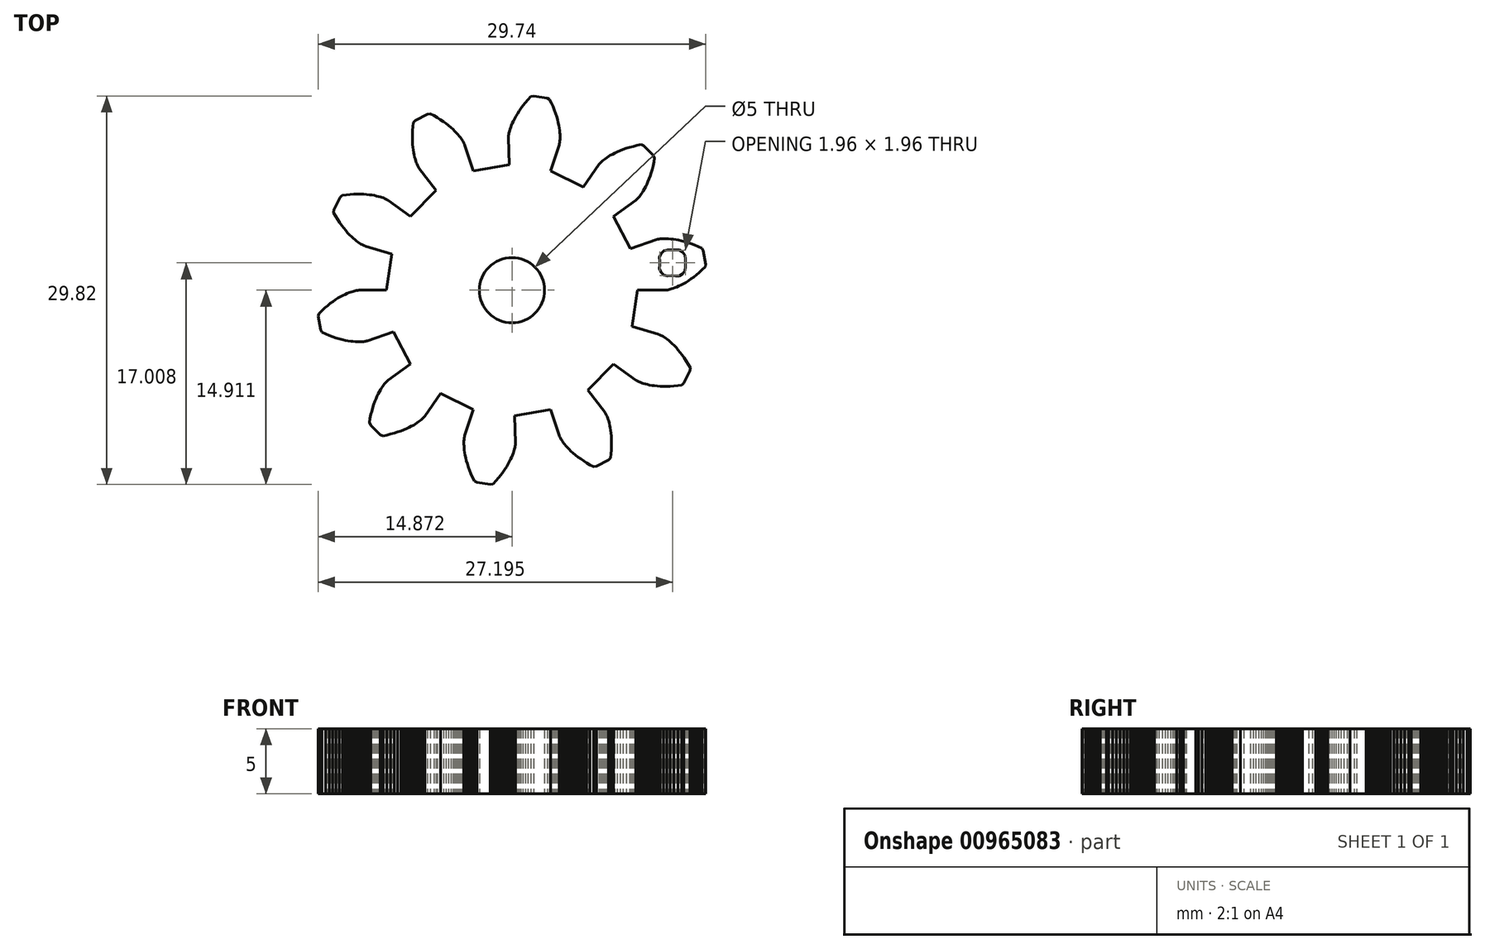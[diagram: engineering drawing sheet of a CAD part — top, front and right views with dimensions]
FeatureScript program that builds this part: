
annotation { "Feature Type Name" : "Feature", "Feature Type Description" : "" }
export const myFeature = defineFeature(function(context is Context, id is Id, definition is map)
    precondition{}
    {
        {
            var Q0;
            Q0=qCreatedBy(makeId("Top.planeOp"),FACE);
            var sketch = newSketch(context, id + "F0", { "sketchPlane" : qUnion([Q0])});
            skLineSegment(sketch, "E0", {"start": v(14.04, 3.47) * mm, "end": v(16.16, 3.47) * mm});
            skLineSegment(sketch, "E1", {"start": v(16.16, 3.47) * mm, "end": v(16.17, 3.47) * mm});
            skLineSegment(sketch, "E2", {"start": v(16.17, 3.47) * mm, "end": v(16.2, 3.47) * mm});
            skLineSegment(sketch, "E3", {"start": v(16.2, 3.47) * mm, "end": v(16.25, 3.48) * mm});
            skLineSegment(sketch, "E4", {"start": v(16.25, 3.48) * mm, "end": v(16.3, 3.49) * mm});
            skLineSegment(sketch, "E5", {"start": v(16.3, 3.49) * mm, "end": v(16.37, 3.5) * mm});
            skLineSegment(sketch, "E6", {"start": v(16.37, 3.5) * mm, "end": v(16.46, 3.52) * mm});
            skLineSegment(sketch, "E7", {"start": v(16.46, 3.52) * mm, "end": v(16.55, 3.54) * mm});
            skLineSegment(sketch, "E8", {"start": v(16.55, 3.54) * mm, "end": v(16.66, 3.57) * mm});
            skLineSegment(sketch, "E9", {"start": v(16.66, 3.57) * mm, "end": v(16.79, 3.61) * mm});
            skLineSegment(sketch, "E10", {"start": v(16.79, 3.61) * mm, "end": v(16.92, 3.66) * mm});
            skLineSegment(sketch, "E11", {"start": v(16.92, 3.66) * mm, "end": v(17.07, 3.72) * mm});
            skLineSegment(sketch, "E12", {"start": v(17.07, 3.72) * mm, "end": v(17.22, 3.8) * mm});
            skLineSegment(sketch, "E13", {"start": v(17.22, 3.8) * mm, "end": v(17.4, 3.87) * mm});
            skLineSegment(sketch, "E14", {"start": v(17.4, 3.87) * mm, "end": v(17.57, 3.97) * mm});
            skLineSegment(sketch, "E15", {"start": v(17.57, 3.97) * mm, "end": v(17.75, 4.07) * mm});
            skLineSegment(sketch, "E16", {"start": v(17.75, 4.07) * mm, "end": v(17.95, 4.2) * mm});
            skLineSegment(sketch, "E17", {"start": v(17.95, 4.2) * mm, "end": v(18.15, 4.33) * mm});
            skLineSegment(sketch, "E18", {"start": v(18.15, 4.33) * mm, "end": v(18.36, 4.48) * mm});
            skLineSegment(sketch, "E19", {"start": v(18.36, 4.48) * mm, "end": v(18.57, 4.65) * mm});
            skLineSegment(sketch, "E20", {"start": v(18.57, 4.65) * mm, "end": v(18.8, 4.83) * mm});
            skLineSegment(sketch, "E21", {"start": v(18.8, 4.83) * mm, "end": v(19.01, 5.04) * mm});
            skLineSegment(sketch, "E22", {"start": v(19.01, 5.04) * mm, "end": v(19.24, 5.25) * mm});
            skLineSegment(sketch, "E23", {"start": v(19.24, 5.25) * mm, "end": v(19.28, 5.47) * mm});
            skLineSegment(sketch, "E24", {"start": v(19.28, 5.47) * mm, "end": v(19.1, 6.5) * mm});
            skLineSegment(sketch, "E25", {"start": v(19.1, 6.5) * mm, "end": v(19, 6.7) * mm});
            skLineSegment(sketch, "E26", {"start": v(19, 6.7) * mm, "end": v(18.71, 6.82) * mm});
            skLineSegment(sketch, "E27", {"start": v(18.71, 6.82) * mm, "end": v(18.43, 6.94) * mm});
            skLineSegment(sketch, "E28", {"start": v(18.43, 6.94) * mm, "end": v(18.17, 7.04) * mm});
            skLineSegment(sketch, "E29", {"start": v(18.17, 7.04) * mm, "end": v(17.9, 7.13) * mm});
            skLineSegment(sketch, "E30", {"start": v(17.9, 7.13) * mm, "end": v(17.66, 7.2) * mm});
            skLineSegment(sketch, "E31", {"start": v(17.66, 7.2) * mm, "end": v(17.43, 7.26) * mm});
            skLineSegment(sketch, "E32", {"start": v(17.43, 7.26) * mm, "end": v(17.2, 7.31) * mm});
            skLineSegment(sketch, "E33", {"start": v(17.2, 7.31) * mm, "end": v(17, 7.35) * mm});
            skLineSegment(sketch, "E34", {"start": v(17, 7.35) * mm, "end": v(16.8, 7.38) * mm});
            skLineSegment(sketch, "E35", {"start": v(16.8, 7.38) * mm, "end": v(16.6, 7.4) * mm});
            skLineSegment(sketch, "E36", {"start": v(16.6, 7.4) * mm, "end": v(16.44, 7.42) * mm});
            skLineSegment(sketch, "E37", {"start": v(16.44, 7.42) * mm, "end": v(16.28, 7.43) * mm});
            skLineSegment(sketch, "E38", {"start": v(16.28, 7.43) * mm, "end": v(16.14, 7.43) * mm});
            skLineSegment(sketch, "E39", {"start": v(16.14, 7.43) * mm, "end": v(16, 7.43) * mm});
            skLineSegment(sketch, "E40", {"start": v(16, 7.43) * mm, "end": v(15.9, 7.42) * mm});
            skLineSegment(sketch, "E41", {"start": v(15.9, 7.42) * mm, "end": v(15.8, 7.41) * mm});
            skLineSegment(sketch, "E42", {"start": v(15.8, 7.41) * mm, "end": v(15.7, 7.4) * mm});
            skLineSegment(sketch, "E43", {"start": v(15.7, 7.4) * mm, "end": v(15.64, 7.39) * mm});
            skLineSegment(sketch, "E44", {"start": v(15.64, 7.39) * mm, "end": v(15.58, 7.38) * mm});
            skLineSegment(sketch, "E45", {"start": v(15.58, 7.38) * mm, "end": v(15.54, 7.37) * mm});
            skLineSegment(sketch, "E46", {"start": v(15.54, 7.37) * mm, "end": v(15.51, 7.36) * mm});
            skLineSegment(sketch, "E47", {"start": v(15.51, 7.36) * mm, "end": v(15.5, 7.36) * mm});
            skLineSegment(sketch, "E48", {"start": v(15.5, 7.36) * mm, "end": v(13.5, 6.65) * mm});
            skLineSegment(sketch, "E49", {"start": v(13.5, 6.65) * mm, "end": v(12.2, 9.13) * mm});
            skLineSegment(sketch, "E50", {"start": v(12.2, 9.13) * mm, "end": v(13.92, 10.38) * mm});
            skLineSegment(sketch, "E51", {"start": v(13.92, 10.38) * mm, "end": v(13.93, 10.39) * mm});
            skLineSegment(sketch, "E52", {"start": v(13.93, 10.39) * mm, "end": v(13.95, 10.4) * mm});
            skLineSegment(sketch, "E53", {"start": v(13.95, 10.4) * mm, "end": v(13.98, 10.43) * mm});
            skLineSegment(sketch, "E54", {"start": v(13.98, 10.43) * mm, "end": v(14.02, 10.47) * mm});
            skLineSegment(sketch, "E55", {"start": v(14.02, 10.47) * mm, "end": v(14.07, 10.52) * mm});
            skLineSegment(sketch, "E56", {"start": v(14.07, 10.52) * mm, "end": v(14.13, 10.59) * mm});
            skLineSegment(sketch, "E57", {"start": v(14.13, 10.59) * mm, "end": v(14.2, 10.66) * mm});
            skLineSegment(sketch, "E58", {"start": v(14.2, 10.66) * mm, "end": v(14.26, 10.75) * mm});
            skLineSegment(sketch, "E59", {"start": v(14.26, 10.75) * mm, "end": v(14.34, 10.86) * mm});
            skLineSegment(sketch, "E60", {"start": v(14.34, 10.86) * mm, "end": v(14.42, 10.98) * mm});
            skLineSegment(sketch, "E61", {"start": v(14.42, 10.98) * mm, "end": v(14.5, 11.11) * mm});
            skLineSegment(sketch, "E62", {"start": v(14.5, 11.11) * mm, "end": v(14.59, 11.26) * mm});
            skLineSegment(sketch, "E63", {"start": v(14.59, 11.26) * mm, "end": v(14.68, 11.42) * mm});
            skLineSegment(sketch, "E64", {"start": v(14.68, 11.42) * mm, "end": v(14.76, 11.6) * mm});
            skLineSegment(sketch, "E65", {"start": v(14.76, 11.6) * mm, "end": v(14.85, 11.8) * mm});
            skLineSegment(sketch, "E66", {"start": v(14.85, 11.8) * mm, "end": v(14.94, 12.01) * mm});
            skLineSegment(sketch, "E67", {"start": v(14.94, 12.01) * mm, "end": v(15.02, 12.24) * mm});
            skLineSegment(sketch, "E68", {"start": v(15.02, 12.24) * mm, "end": v(15.1, 12.49) * mm});
            skLineSegment(sketch, "E69", {"start": v(15.1, 12.49) * mm, "end": v(15.17, 12.75) * mm});
            skLineSegment(sketch, "E70", {"start": v(15.17, 12.75) * mm, "end": v(15.24, 13.03) * mm});
            skLineSegment(sketch, "E71", {"start": v(15.24, 13.03) * mm, "end": v(15.3, 13.32) * mm});
            skLineSegment(sketch, "E72", {"start": v(15.3, 13.32) * mm, "end": v(15.36, 13.63) * mm});
            skLineSegment(sketch, "E73", {"start": v(15.36, 13.63) * mm, "end": v(15.27, 13.82) * mm});
            skLineSegment(sketch, "E74", {"start": v(15.27, 13.82) * mm, "end": v(14.51, 14.56) * mm});
            skLineSegment(sketch, "E75", {"start": v(14.51, 14.56) * mm, "end": v(14.32, 14.65) * mm});
            skLineSegment(sketch, "E76", {"start": v(14.32, 14.65) * mm, "end": v(14, 14.59) * mm});
            skLineSegment(sketch, "E77", {"start": v(14, 14.59) * mm, "end": v(13.72, 14.52) * mm});
            skLineSegment(sketch, "E78", {"start": v(13.72, 14.52) * mm, "end": v(13.44, 14.44) * mm});
            skLineSegment(sketch, "E79", {"start": v(13.44, 14.44) * mm, "end": v(13.18, 14.36) * mm});
            skLineSegment(sketch, "E80", {"start": v(13.18, 14.36) * mm, "end": v(12.94, 14.28) * mm});
            skLineSegment(sketch, "E81", {"start": v(12.94, 14.28) * mm, "end": v(12.71, 14.19) * mm});
            skLineSegment(sketch, "E82", {"start": v(12.71, 14.19) * mm, "end": v(12.5, 14.1) * mm});
            skLineSegment(sketch, "E83", {"start": v(12.5, 14.1) * mm, "end": v(12.3, 14) * mm});
            skLineSegment(sketch, "E84", {"start": v(12.3, 14) * mm, "end": v(12.13, 13.91) * mm});
            skLineSegment(sketch, "E85", {"start": v(12.13, 13.91) * mm, "end": v(11.97, 13.82) * mm});
            skLineSegment(sketch, "E86", {"start": v(11.97, 13.82) * mm, "end": v(11.82, 13.73) * mm});
            skLineSegment(sketch, "E87", {"start": v(11.82, 13.73) * mm, "end": v(11.69, 13.65) * mm});
            skLineSegment(sketch, "E88", {"start": v(11.69, 13.65) * mm, "end": v(11.57, 13.57) * mm});
            skLineSegment(sketch, "E89", {"start": v(11.57, 13.57) * mm, "end": v(11.47, 13.49) * mm});
            skLineSegment(sketch, "E90", {"start": v(11.47, 13.49) * mm, "end": v(11.38, 13.42) * mm});
            skLineSegment(sketch, "E91", {"start": v(11.38, 13.42) * mm, "end": v(11.3, 13.35) * mm});
            skLineSegment(sketch, "E92", {"start": v(11.3, 13.35) * mm, "end": v(11.24, 13.29) * mm});
            skLineSegment(sketch, "E93", {"start": v(11.24, 13.29) * mm, "end": v(11.2, 13.24) * mm});
            skLineSegment(sketch, "E94", {"start": v(11.2, 13.24) * mm, "end": v(11.15, 13.2) * mm});
            skLineSegment(sketch, "E95", {"start": v(11.15, 13.2) * mm, "end": v(11.12, 13.16) * mm});
            skLineSegment(sketch, "E96", {"start": v(11.12, 13.16) * mm, "end": v(11.1, 13.14) * mm});
            skLineSegment(sketch, "E97", {"start": v(11.1, 13.14) * mm, "end": v(11.1, 13.13) * mm});
            skLineSegment(sketch, "E98", {"start": v(11.1, 13.13) * mm, "end": v(9.9, 11.39) * mm});
            skLineSegment(sketch, "E99", {"start": v(9.9, 11.39) * mm, "end": v(7.39, 12.63) * mm});
            skLineSegment(sketch, "E100", {"start": v(7.39, 12.63) * mm, "end": v(8.04, 14.64) * mm});
            skLineSegment(sketch, "E101", {"start": v(8.04, 14.64) * mm, "end": v(8.05, 14.66) * mm});
            skLineSegment(sketch, "E102", {"start": v(8.05, 14.66) * mm, "end": v(8.05, 14.69) * mm});
            skLineSegment(sketch, "E103", {"start": v(8.05, 14.69) * mm, "end": v(8.06, 14.73) * mm});
            skLineSegment(sketch, "E104", {"start": v(8.06, 14.73) * mm, "end": v(8.07, 14.78) * mm});
            skLineSegment(sketch, "E105", {"start": v(8.07, 14.78) * mm, "end": v(8.08, 14.86) * mm});
            skLineSegment(sketch, "E106", {"start": v(8.08, 14.86) * mm, "end": v(8.1, 14.94) * mm});
            skLineSegment(sketch, "E107", {"start": v(8.1, 14.94) * mm, "end": v(8.1, 15.04) * mm});
            skLineSegment(sketch, "E108", {"start": v(8.1, 15.04) * mm, "end": v(8.1, 15.15) * mm});
            skLineSegment(sketch, "E109", {"start": v(8.1, 15.15) * mm, "end": v(8.1, 15.28) * mm});
            skLineSegment(sketch, "E110", {"start": v(8.1, 15.28) * mm, "end": v(8.1, 15.43) * mm});
            skLineSegment(sketch, "E111", {"start": v(8.1, 15.43) * mm, "end": v(8.09, 15.58) * mm});
            skLineSegment(sketch, "E112", {"start": v(8.09, 15.58) * mm, "end": v(8.07, 15.75) * mm});
            skLineSegment(sketch, "E113", {"start": v(8.07, 15.75) * mm, "end": v(8.04, 15.94) * mm});
            skLineSegment(sketch, "E114", {"start": v(8.04, 15.94) * mm, "end": v(8, 16.14) * mm});
            skLineSegment(sketch, "E115", {"start": v(8, 16.14) * mm, "end": v(7.96, 16.35) * mm});
            skLineSegment(sketch, "E116", {"start": v(7.96, 16.35) * mm, "end": v(7.9, 16.57) * mm});
            skLineSegment(sketch, "E117", {"start": v(7.9, 16.57) * mm, "end": v(7.84, 16.8) * mm});
            skLineSegment(sketch, "E118", {"start": v(7.84, 16.8) * mm, "end": v(7.76, 17.05) * mm});
            skLineSegment(sketch, "E119", {"start": v(7.76, 17.05) * mm, "end": v(7.67, 17.3) * mm});
            skLineSegment(sketch, "E120", {"start": v(7.67, 17.3) * mm, "end": v(7.56, 17.57) * mm});
            skLineSegment(sketch, "E121", {"start": v(7.56, 17.57) * mm, "end": v(7.44, 17.84) * mm});
            skLineSegment(sketch, "E122", {"start": v(7.44, 17.84) * mm, "end": v(7.3, 18.13) * mm});
            skLineSegment(sketch, "E123", {"start": v(7.3, 18.13) * mm, "end": v(7.1, 18.23) * mm});
            skLineSegment(sketch, "E124", {"start": v(7.1, 18.23) * mm, "end": v(6.07, 18.38) * mm});
            skLineSegment(sketch, "E125", {"start": v(6.07, 18.38) * mm, "end": v(5.86, 18.34) * mm});
            skLineSegment(sketch, "E126", {"start": v(5.86, 18.34) * mm, "end": v(5.64, 18.1) * mm});
            skLineSegment(sketch, "E127", {"start": v(5.64, 18.1) * mm, "end": v(5.45, 17.88) * mm});
            skLineSegment(sketch, "E128", {"start": v(5.45, 17.88) * mm, "end": v(5.27, 17.65) * mm});
            skLineSegment(sketch, "E129", {"start": v(5.27, 17.65) * mm, "end": v(5.1, 17.44) * mm});
            skLineSegment(sketch, "E130", {"start": v(5.1, 17.44) * mm, "end": v(4.96, 17.22) * mm});
            skLineSegment(sketch, "E131", {"start": v(4.96, 17.22) * mm, "end": v(4.83, 17.02) * mm});
            skLineSegment(sketch, "E132", {"start": v(4.83, 17.02) * mm, "end": v(4.7, 16.82) * mm});
            skLineSegment(sketch, "E133", {"start": v(4.7, 16.82) * mm, "end": v(4.6, 16.64) * mm});
            skLineSegment(sketch, "E134", {"start": v(4.6, 16.64) * mm, "end": v(4.52, 16.46) * mm});
            skLineSegment(sketch, "E135", {"start": v(4.52, 16.46) * mm, "end": v(4.44, 16.29) * mm});
            skLineSegment(sketch, "E136", {"start": v(4.44, 16.29) * mm, "end": v(4.37, 16.13) * mm});
            skLineSegment(sketch, "E137", {"start": v(4.37, 16.13) * mm, "end": v(4.32, 15.98) * mm});
            skLineSegment(sketch, "E138", {"start": v(4.32, 15.98) * mm, "end": v(4.27, 15.85) * mm});
            skLineSegment(sketch, "E139", {"start": v(4.27, 15.85) * mm, "end": v(4.23, 15.72) * mm});
            skLineSegment(sketch, "E140", {"start": v(4.23, 15.72) * mm, "end": v(4.2, 15.61) * mm});
            skLineSegment(sketch, "E141", {"start": v(4.2, 15.61) * mm, "end": v(4.18, 15.51) * mm});
            skLineSegment(sketch, "E142", {"start": v(4.18, 15.51) * mm, "end": v(4.17, 15.43) * mm});
            skLineSegment(sketch, "E143", {"start": v(4.17, 15.43) * mm, "end": v(4.16, 15.36) * mm});
            skLineSegment(sketch, "E144", {"start": v(4.16, 15.36) * mm, "end": v(4.15, 15.3) * mm});
            skLineSegment(sketch, "E145", {"start": v(4.15, 15.3) * mm, "end": v(4.15, 15.26) * mm});
            skLineSegment(sketch, "E146", {"start": v(4.15, 15.26) * mm, "end": v(4.14, 15.23) * mm});
            skLineSegment(sketch, "E147", {"start": v(4.14, 15.23) * mm, "end": v(4.14, 15.22) * mm});
            skLineSegment(sketch, "E148", {"start": v(4.14, 15.22) * mm, "end": v(4.2, 13.1) * mm});
            skLineSegment(sketch, "E149", {"start": v(4.2, 13.1) * mm, "end": v(1.44, 12.63) * mm});
            skLineSegment(sketch, "E150", {"start": v(1.44, 12.63) * mm, "end": v(0.78, 14.64) * mm});
            skLineSegment(sketch, "E151", {"start": v(0.78, 14.64) * mm, "end": v(0.78, 14.66) * mm});
            skLineSegment(sketch, "E152", {"start": v(0.78, 14.66) * mm, "end": v(0.77, 14.68) * mm});
            skLineSegment(sketch, "E153", {"start": v(0.77, 14.68) * mm, "end": v(0.75, 14.72) * mm});
            skLineSegment(sketch, "E154", {"start": v(0.75, 14.72) * mm, "end": v(0.72, 14.77) * mm});
            skLineSegment(sketch, "E155", {"start": v(0.72, 14.77) * mm, "end": v(0.69, 14.84) * mm});
            skLineSegment(sketch, "E156", {"start": v(0.69, 14.84) * mm, "end": v(0.65, 14.91) * mm});
            skLineSegment(sketch, "E157", {"start": v(0.65, 14.91) * mm, "end": v(0.6, 15) * mm});
            skLineSegment(sketch, "E158", {"start": v(0.6, 15) * mm, "end": v(0.53, 15.1) * mm});
            skLineSegment(sketch, "E159", {"start": v(0.53, 15.1) * mm, "end": v(0.45, 15.2) * mm});
            skLineSegment(sketch, "E160", {"start": v(0.45, 15.2) * mm, "end": v(0.37, 15.3) * mm});
            skLineSegment(sketch, "E161", {"start": v(0.37, 15.3) * mm, "end": v(0.26, 15.43) * mm});
            skLineSegment(sketch, "E162", {"start": v(0.26, 15.43) * mm, "end": v(0.15, 15.56) * mm});
            skLineSegment(sketch, "E163", {"start": v(0.15, 15.56) * mm, "end": v(0.02, 15.7) * mm});
            skLineSegment(sketch, "E164", {"start": v(0.02, 15.7) * mm, "end": v(-0.12, 15.83) * mm});
            skLineSegment(sketch, "E165", {"start": v(-0.12, 15.83) * mm, "end": v(-0.28, 15.97) * mm});
            skLineSegment(sketch, "E166", {"start": v(-0.28, 15.97) * mm, "end": v(-0.46, 16.12) * mm});
            skLineSegment(sketch, "E167", {"start": v(-0.46, 16.12) * mm, "end": v(-0.65, 16.27) * mm});
            skLineSegment(sketch, "E168", {"start": v(-0.65, 16.27) * mm, "end": v(-0.86, 16.42) * mm});
            skLineSegment(sketch, "E169", {"start": v(-0.86, 16.42) * mm, "end": v(-1.09, 16.57) * mm});
            skLineSegment(sketch, "E170", {"start": v(-1.09, 16.57) * mm, "end": v(-1.33, 16.73) * mm});
            skLineSegment(sketch, "E171", {"start": v(-1.33, 16.73) * mm, "end": v(-1.59, 16.88) * mm});
            skLineSegment(sketch, "E172", {"start": v(-1.59, 16.88) * mm, "end": v(-1.87, 17.02) * mm});
            skLineSegment(sketch, "E173", {"start": v(-1.87, 17.02) * mm, "end": v(-2.08, 17) * mm});
            skLineSegment(sketch, "E174", {"start": v(-2.08, 17) * mm, "end": v(-3.01, 16.5) * mm});
            skLineSegment(sketch, "E175", {"start": v(-3.01, 16.5) * mm, "end": v(-3.16, 16.35) * mm});
            skLineSegment(sketch, "E176", {"start": v(-3.16, 16.35) * mm, "end": v(-3.2, 16.03) * mm});
            skLineSegment(sketch, "E177", {"start": v(-3.2, 16.03) * mm, "end": v(-3.22, 15.73) * mm});
            skLineSegment(sketch, "E178", {"start": v(-3.22, 15.73) * mm, "end": v(-3.23, 15.45) * mm});
            skLineSegment(sketch, "E179", {"start": v(-3.23, 15.45) * mm, "end": v(-3.24, 15.18) * mm});
            skLineSegment(sketch, "E180", {"start": v(-3.24, 15.18) * mm, "end": v(-3.23, 14.92) * mm});
            skLineSegment(sketch, "E181", {"start": v(-3.23, 14.92) * mm, "end": v(-3.22, 14.68) * mm});
            skLineSegment(sketch, "E182", {"start": v(-3.22, 14.68) * mm, "end": v(-3.2, 14.45) * mm});
            skLineSegment(sketch, "E183", {"start": v(-3.2, 14.45) * mm, "end": v(-3.17, 14.24) * mm});
            skLineSegment(sketch, "E184", {"start": v(-3.17, 14.24) * mm, "end": v(-3.14, 14.04) * mm});
            skLineSegment(sketch, "E185", {"start": v(-3.14, 14.04) * mm, "end": v(-3.1, 13.86) * mm});
            skLineSegment(sketch, "E186", {"start": v(-3.1, 13.86) * mm, "end": v(-3.06, 13.69) * mm});
            skLineSegment(sketch, "E187", {"start": v(-3.06, 13.69) * mm, "end": v(-3.02, 13.54) * mm});
            skLineSegment(sketch, "E188", {"start": v(-3.02, 13.54) * mm, "end": v(-2.98, 13.4) * mm});
            skLineSegment(sketch, "E189", {"start": v(-2.98, 13.4) * mm, "end": v(-2.93, 13.28) * mm});
            skLineSegment(sketch, "E190", {"start": v(-2.93, 13.28) * mm, "end": v(-2.9, 13.17) * mm});
            skLineSegment(sketch, "E191", {"start": v(-2.9, 13.17) * mm, "end": v(-2.85, 13.08) * mm});
            skLineSegment(sketch, "E192", {"start": v(-2.85, 13.08) * mm, "end": v(-2.82, 13) * mm});
            skLineSegment(sketch, "E193", {"start": v(-2.82, 13) * mm, "end": v(-2.78, 12.94) * mm});
            skLineSegment(sketch, "E194", {"start": v(-2.78, 12.94) * mm, "end": v(-2.75, 12.89) * mm});
            skLineSegment(sketch, "E195", {"start": v(-2.75, 12.89) * mm, "end": v(-2.73, 12.85) * mm});
            skLineSegment(sketch, "E196", {"start": v(-2.73, 12.85) * mm, "end": v(-2.72, 12.83) * mm});
            skLineSegment(sketch, "E197", {"start": v(-2.72, 12.83) * mm, "end": v(-2.7, 12.82) * mm});
            skLineSegment(sketch, "E198", {"start": v(-2.7, 12.82) * mm, "end": v(-1.42, 11.13) * mm});
            skLineSegment(sketch, "E199", {"start": v(-1.42, 11.13) * mm, "end": v(-3.38, 9.13) * mm});
            skLineSegment(sketch, "E200", {"start": v(-3.38, 9.13) * mm, "end": v(-5.1, 10.38) * mm});
            skLineSegment(sketch, "E201", {"start": v(-5.1, 10.38) * mm, "end": v(-5.1, 10.38) * mm});
            skLineSegment(sketch, "E202", {"start": v(-5.1, 10.38) * mm, "end": v(-5.13, 10.4) * mm});
            skLineSegment(sketch, "E203", {"start": v(-5.13, 10.4) * mm, "end": v(-5.17, 10.42) * mm});
            skLineSegment(sketch, "E204", {"start": v(-5.17, 10.42) * mm, "end": v(-5.22, 10.45) * mm});
            skLineSegment(sketch, "E205", {"start": v(-5.22, 10.45) * mm, "end": v(-5.28, 10.48) * mm});
            skLineSegment(sketch, "E206", {"start": v(-5.28, 10.48) * mm, "end": v(-5.36, 10.51) * mm});
            skLineSegment(sketch, "E207", {"start": v(-5.36, 10.51) * mm, "end": v(-5.45, 10.55) * mm});
            skLineSegment(sketch, "E208", {"start": v(-5.45, 10.55) * mm, "end": v(-5.56, 10.6) * mm});
            skLineSegment(sketch, "E209", {"start": v(-5.56, 10.6) * mm, "end": v(-5.68, 10.63) * mm});
            skLineSegment(sketch, "E210", {"start": v(-5.68, 10.63) * mm, "end": v(-5.82, 10.67) * mm});
            skLineSegment(sketch, "E211", {"start": v(-5.82, 10.67) * mm, "end": v(-5.97, 10.7) * mm});
            skLineSegment(sketch, "E212", {"start": v(-5.97, 10.7) * mm, "end": v(-6.14, 10.74) * mm});
            skLineSegment(sketch, "E213", {"start": v(-6.14, 10.74) * mm, "end": v(-6.32, 10.78) * mm});
            skLineSegment(sketch, "E214", {"start": v(-6.32, 10.78) * mm, "end": v(-6.52, 10.8) * mm});
            skLineSegment(sketch, "E215", {"start": v(-6.52, 10.8) * mm, "end": v(-6.74, 10.83) * mm});
            skLineSegment(sketch, "E216", {"start": v(-6.74, 10.83) * mm, "end": v(-6.96, 10.84) * mm});
            skLineSegment(sketch, "E217", {"start": v(-6.96, 10.84) * mm, "end": v(-7.2, 10.85) * mm});
            skLineSegment(sketch, "E218", {"start": v(-7.2, 10.85) * mm, "end": v(-7.47, 10.85) * mm});
            skLineSegment(sketch, "E219", {"start": v(-7.47, 10.85) * mm, "end": v(-7.74, 10.84) * mm});
            skLineSegment(sketch, "E220", {"start": v(-7.74, 10.84) * mm, "end": v(-8.02, 10.82) * mm});
            skLineSegment(sketch, "E221", {"start": v(-8.02, 10.82) * mm, "end": v(-8.32, 10.79) * mm});
            skLineSegment(sketch, "E222", {"start": v(-8.32, 10.79) * mm, "end": v(-8.63, 10.75) * mm});
            skLineSegment(sketch, "E223", {"start": v(-8.63, 10.75) * mm, "end": v(-8.79, 10.6) * mm});
            skLineSegment(sketch, "E224", {"start": v(-8.79, 10.6) * mm, "end": v(-9.26, 9.65) * mm});
            skLineSegment(sketch, "E225", {"start": v(-9.26, 9.65) * mm, "end": v(-9.28, 9.44) * mm});
            skLineSegment(sketch, "E226", {"start": v(-9.28, 9.44) * mm, "end": v(-9.13, 9.16) * mm});
            skLineSegment(sketch, "E227", {"start": v(-9.13, 9.16) * mm, "end": v(-8.97, 8.9) * mm});
            skLineSegment(sketch, "E228", {"start": v(-8.97, 8.9) * mm, "end": v(-8.81, 8.67) * mm});
            skLineSegment(sketch, "E229", {"start": v(-8.81, 8.67) * mm, "end": v(-8.66, 8.45) * mm});
            skLineSegment(sketch, "E230", {"start": v(-8.66, 8.45) * mm, "end": v(-8.5, 8.24) * mm});
            skLineSegment(sketch, "E231", {"start": v(-8.5, 8.24) * mm, "end": v(-8.35, 8.05) * mm});
            skLineSegment(sketch, "E232", {"start": v(-8.35, 8.05) * mm, "end": v(-8.2, 7.88) * mm});
            skLineSegment(sketch, "E233", {"start": v(-8.2, 7.88) * mm, "end": v(-8.05, 7.72) * mm});
            skLineSegment(sketch, "E234", {"start": v(-8.05, 7.72) * mm, "end": v(-7.9, 7.58) * mm});
            skLineSegment(sketch, "E235", {"start": v(-7.9, 7.58) * mm, "end": v(-7.77, 7.46) * mm});
            skLineSegment(sketch, "E236", {"start": v(-7.77, 7.46) * mm, "end": v(-7.64, 7.35) * mm});
            skLineSegment(sketch, "E237", {"start": v(-7.64, 7.35) * mm, "end": v(-7.52, 7.25) * mm});
            skLineSegment(sketch, "E238", {"start": v(-7.52, 7.25) * mm, "end": v(-7.4, 7.16) * mm});
            skLineSegment(sketch, "E239", {"start": v(-7.4, 7.16) * mm, "end": v(-7.3, 7.09) * mm});
            skLineSegment(sketch, "E240", {"start": v(-7.3, 7.09) * mm, "end": v(-7.2, 7.03) * mm});
            skLineSegment(sketch, "E241", {"start": v(-7.2, 7.03) * mm, "end": v(-7.11, 6.97) * mm});
            skLineSegment(sketch, "E242", {"start": v(-7.11, 6.97) * mm, "end": v(-7.04, 6.93) * mm});
            skLineSegment(sketch, "E243", {"start": v(-7.04, 6.93) * mm, "end": v(-6.97, 6.9) * mm});
            skLineSegment(sketch, "E244", {"start": v(-6.97, 6.9) * mm, "end": v(-6.92, 6.88) * mm});
            skLineSegment(sketch, "E245", {"start": v(-6.92, 6.88) * mm, "end": v(-6.88, 6.86) * mm});
            skLineSegment(sketch, "E246", {"start": v(-6.88, 6.86) * mm, "end": v(-6.85, 6.85) * mm});
            skLineSegment(sketch, "E247", {"start": v(-6.85, 6.85) * mm, "end": v(-6.84, 6.85) * mm});
            skLineSegment(sketch, "E248", {"start": v(-6.84, 6.85) * mm, "end": v(-4.8, 6.24) * mm});
            skLineSegment(sketch, "E249", {"start": v(-4.8, 6.24) * mm, "end": v(-5.21, 3.47) * mm});
            skLineSegment(sketch, "E250", {"start": v(-5.21, 3.47) * mm, "end": v(-7.34, 3.47) * mm});
            skLineSegment(sketch, "E251", {"start": v(-7.34, 3.47) * mm, "end": v(-7.35, 3.47) * mm});
            skLineSegment(sketch, "E252", {"start": v(-7.35, 3.47) * mm, "end": v(-7.38, 3.47) * mm});
            skLineSegment(sketch, "E253", {"start": v(-7.38, 3.47) * mm, "end": v(-7.42, 3.46) * mm});
            skLineSegment(sketch, "E254", {"start": v(-7.42, 3.46) * mm, "end": v(-7.48, 3.46) * mm});
            skLineSegment(sketch, "E255", {"start": v(-7.48, 3.46) * mm, "end": v(-7.55, 3.44) * mm});
            skLineSegment(sketch, "E256", {"start": v(-7.55, 3.44) * mm, "end": v(-7.63, 3.43) * mm});
            skLineSegment(sketch, "E257", {"start": v(-7.63, 3.43) * mm, "end": v(-7.73, 3.4) * mm});
            skLineSegment(sketch, "E258", {"start": v(-7.73, 3.4) * mm, "end": v(-7.84, 3.37) * mm});
            skLineSegment(sketch, "E259", {"start": v(-7.84, 3.37) * mm, "end": v(-7.96, 3.33) * mm});
            skLineSegment(sketch, "E260", {"start": v(-7.96, 3.33) * mm, "end": v(-8.1, 3.28) * mm});
            skLineSegment(sketch, "E261", {"start": v(-8.1, 3.28) * mm, "end": v(-8.24, 3.22) * mm});
            skLineSegment(sketch, "E262", {"start": v(-8.24, 3.22) * mm, "end": v(-8.4, 3.15) * mm});
            skLineSegment(sketch, "E263", {"start": v(-8.4, 3.15) * mm, "end": v(-8.57, 3.07) * mm});
            skLineSegment(sketch, "E264", {"start": v(-8.57, 3.07) * mm, "end": v(-8.74, 2.98) * mm});
            skLineSegment(sketch, "E265", {"start": v(-8.74, 2.98) * mm, "end": v(-8.93, 2.87) * mm});
            skLineSegment(sketch, "E266", {"start": v(-8.93, 2.87) * mm, "end": v(-9.12, 2.75) * mm});
            skLineSegment(sketch, "E267", {"start": v(-9.12, 2.75) * mm, "end": v(-9.33, 2.61) * mm});
            skLineSegment(sketch, "E268", {"start": v(-9.33, 2.61) * mm, "end": v(-9.53, 2.46) * mm});
            skLineSegment(sketch, "E269", {"start": v(-9.53, 2.46) * mm, "end": v(-9.75, 2.3) * mm});
            skLineSegment(sketch, "E270", {"start": v(-9.75, 2.3) * mm, "end": v(-9.97, 2.1) * mm});
            skLineSegment(sketch, "E271", {"start": v(-9.97, 2.1) * mm, "end": v(-10.2, 1.9) * mm});
            skLineSegment(sketch, "E272", {"start": v(-10.2, 1.9) * mm, "end": v(-10.42, 1.69) * mm});
            skLineSegment(sketch, "E273", {"start": v(-10.42, 1.69) * mm, "end": v(-10.46, 1.48) * mm});
            skLineSegment(sketch, "E274", {"start": v(-10.46, 1.48) * mm, "end": v(-10.28, 0.44) * mm});
            skLineSegment(sketch, "E275", {"start": v(-10.28, 0.44) * mm, "end": v(-10.17, 0.25) * mm});
            skLineSegment(sketch, "E276", {"start": v(-10.17, 0.25) * mm, "end": v(-9.89, 0.12) * mm});
            skLineSegment(sketch, "E277", {"start": v(-9.89, 0.12) * mm, "end": v(-9.6, 0) * mm});
            skLineSegment(sketch, "E278", {"start": v(-9.6, 0) * mm, "end": v(-9.34, -0.1) * mm});
            skLineSegment(sketch, "E279", {"start": v(-9.34, -0.1) * mm, "end": v(-9.08, -0.19) * mm});
            skLineSegment(sketch, "E280", {"start": v(-9.08, -0.19) * mm, "end": v(-8.84, -0.26) * mm});
            skLineSegment(sketch, "E281", {"start": v(-8.84, -0.26) * mm, "end": v(-8.6, -0.32) * mm});
            skLineSegment(sketch, "E282", {"start": v(-8.6, -0.32) * mm, "end": v(-8.38, -0.37) * mm});
            skLineSegment(sketch, "E283", {"start": v(-8.38, -0.37) * mm, "end": v(-8.17, -0.41) * mm});
            skLineSegment(sketch, "E284", {"start": v(-8.17, -0.41) * mm, "end": v(-7.97, -0.44) * mm});
            skLineSegment(sketch, "E285", {"start": v(-7.97, -0.44) * mm, "end": v(-7.79, -0.46) * mm});
            skLineSegment(sketch, "E286", {"start": v(-7.79, -0.46) * mm, "end": v(-7.61, -0.48) * mm});
            skLineSegment(sketch, "E287", {"start": v(-7.61, -0.48) * mm, "end": v(-7.46, -0.48) * mm});
            skLineSegment(sketch, "E288", {"start": v(-7.46, -0.48) * mm, "end": v(-7.31, -0.49) * mm});
            skLineSegment(sketch, "E289", {"start": v(-7.31, -0.49) * mm, "end": v(-7.18, -0.48) * mm});
            skLineSegment(sketch, "E290", {"start": v(-7.18, -0.48) * mm, "end": v(-7.07, -0.48) * mm});
            skLineSegment(sketch, "E291", {"start": v(-7.07, -0.48) * mm, "end": v(-6.97, -0.47) * mm});
            skLineSegment(sketch, "E292", {"start": v(-6.97, -0.47) * mm, "end": v(-6.89, -0.46) * mm});
            skLineSegment(sketch, "E293", {"start": v(-6.89, -0.46) * mm, "end": v(-6.81, -0.45) * mm});
            skLineSegment(sketch, "E294", {"start": v(-6.81, -0.45) * mm, "end": v(-6.76, -0.43) * mm});
            skLineSegment(sketch, "E295", {"start": v(-6.76, -0.43) * mm, "end": v(-6.72, -0.42) * mm});
            skLineSegment(sketch, "E296", {"start": v(-6.72, -0.42) * mm, "end": v(-6.69, -0.42) * mm});
            skLineSegment(sketch, "E297", {"start": v(-6.69, -0.42) * mm, "end": v(-6.68, -0.41) * mm});
            skLineSegment(sketch, "E298", {"start": v(-6.68, -0.41) * mm, "end": v(-4.67, 0.29) * mm});
            skLineSegment(sketch, "E299", {"start": v(-4.67, 0.29) * mm, "end": v(-3.38, -2.19) * mm});
            skLineSegment(sketch, "E300", {"start": v(-3.38, -2.19) * mm, "end": v(-5.1, -3.43) * mm});
            skLineSegment(sketch, "E301", {"start": v(-5.1, -3.43) * mm, "end": v(-5.1, -3.44) * mm});
            skLineSegment(sketch, "E302", {"start": v(-5.1, -3.44) * mm, "end": v(-5.13, -3.46) * mm});
            skLineSegment(sketch, "E303", {"start": v(-5.13, -3.46) * mm, "end": v(-5.16, -3.49) * mm});
            skLineSegment(sketch, "E304", {"start": v(-5.16, -3.49) * mm, "end": v(-5.2, -3.53) * mm});
            skLineSegment(sketch, "E305", {"start": v(-5.2, -3.53) * mm, "end": v(-5.25, -3.58) * mm});
            skLineSegment(sketch, "E306", {"start": v(-5.25, -3.58) * mm, "end": v(-5.3, -3.65) * mm});
            skLineSegment(sketch, "E307", {"start": v(-5.3, -3.65) * mm, "end": v(-5.37, -3.72) * mm});
            skLineSegment(sketch, "E308", {"start": v(-5.37, -3.72) * mm, "end": v(-5.44, -3.81) * mm});
            skLineSegment(sketch, "E309", {"start": v(-5.44, -3.81) * mm, "end": v(-5.52, -3.92) * mm});
            skLineSegment(sketch, "E310", {"start": v(-5.52, -3.92) * mm, "end": v(-5.6, -4.04) * mm});
            skLineSegment(sketch, "E311", {"start": v(-5.6, -4.04) * mm, "end": v(-5.68, -4.17) * mm});
            skLineSegment(sketch, "E312", {"start": v(-5.68, -4.17) * mm, "end": v(-5.77, -4.32) * mm});
            skLineSegment(sketch, "E313", {"start": v(-5.77, -4.32) * mm, "end": v(-5.85, -4.48) * mm});
            skLineSegment(sketch, "E314", {"start": v(-5.85, -4.48) * mm, "end": v(-5.94, -4.66) * mm});
            skLineSegment(sketch, "E315", {"start": v(-5.94, -4.66) * mm, "end": v(-6.03, -4.86) * mm});
            skLineSegment(sketch, "E316", {"start": v(-6.03, -4.86) * mm, "end": v(-6.11, -5.07) * mm});
            skLineSegment(sketch, "E317", {"start": v(-6.11, -5.07) * mm, "end": v(-6.2, -5.3) * mm});
            skLineSegment(sketch, "E318", {"start": v(-6.2, -5.3) * mm, "end": v(-6.28, -5.54) * mm});
            skLineSegment(sketch, "E319", {"start": v(-6.28, -5.54) * mm, "end": v(-6.35, -5.8) * mm});
            skLineSegment(sketch, "E320", {"start": v(-6.35, -5.8) * mm, "end": v(-6.42, -6.08) * mm});
            skLineSegment(sketch, "E321", {"start": v(-6.42, -6.08) * mm, "end": v(-6.48, -6.38) * mm});
            skLineSegment(sketch, "E322", {"start": v(-6.48, -6.38) * mm, "end": v(-6.54, -6.69) * mm});
            skLineSegment(sketch, "E323", {"start": v(-6.54, -6.69) * mm, "end": v(-6.44, -6.88) * mm});
            skLineSegment(sketch, "E324", {"start": v(-6.44, -6.88) * mm, "end": v(-5.69, -7.62) * mm});
            skLineSegment(sketch, "E325", {"start": v(-5.69, -7.62) * mm, "end": v(-5.5, -7.7) * mm});
            skLineSegment(sketch, "E326", {"start": v(-5.5, -7.7) * mm, "end": v(-5.19, -7.65) * mm});
            skLineSegment(sketch, "E327", {"start": v(-5.19, -7.65) * mm, "end": v(-4.9, -7.58) * mm});
            skLineSegment(sketch, "E328", {"start": v(-4.9, -7.58) * mm, "end": v(-4.62, -7.5) * mm});
            skLineSegment(sketch, "E329", {"start": v(-4.62, -7.5) * mm, "end": v(-4.36, -7.42) * mm});
            skLineSegment(sketch, "E330", {"start": v(-4.36, -7.42) * mm, "end": v(-4.11, -7.33) * mm});
            skLineSegment(sketch, "E331", {"start": v(-4.11, -7.33) * mm, "end": v(-3.89, -7.25) * mm});
            skLineSegment(sketch, "E332", {"start": v(-3.89, -7.25) * mm, "end": v(-3.68, -7.16) * mm});
            skLineSegment(sketch, "E333", {"start": v(-3.68, -7.16) * mm, "end": v(-3.48, -7.06) * mm});
            skLineSegment(sketch, "E334", {"start": v(-3.48, -7.06) * mm, "end": v(-3.3, -6.97) * mm});
            skLineSegment(sketch, "E335", {"start": v(-3.3, -6.97) * mm, "end": v(-3.14, -6.88) * mm});
            skLineSegment(sketch, "E336", {"start": v(-3.14, -6.88) * mm, "end": v(-3, -6.8) * mm});
            skLineSegment(sketch, "E337", {"start": v(-3, -6.8) * mm, "end": v(-2.86, -6.7) * mm});
            skLineSegment(sketch, "E338", {"start": v(-2.86, -6.7) * mm, "end": v(-2.75, -6.62) * mm});
            skLineSegment(sketch, "E339", {"start": v(-2.75, -6.62) * mm, "end": v(-2.65, -6.54) * mm});
            skLineSegment(sketch, "E340", {"start": v(-2.65, -6.54) * mm, "end": v(-2.56, -6.47) * mm});
            skLineSegment(sketch, "E341", {"start": v(-2.56, -6.47) * mm, "end": v(-2.48, -6.4) * mm});
            skLineSegment(sketch, "E342", {"start": v(-2.48, -6.4) * mm, "end": v(-2.42, -6.35) * mm});
            skLineSegment(sketch, "E343", {"start": v(-2.42, -6.35) * mm, "end": v(-2.37, -6.3) * mm});
            skLineSegment(sketch, "E344", {"start": v(-2.37, -6.3) * mm, "end": v(-2.33, -6.25) * mm});
            skLineSegment(sketch, "E345", {"start": v(-2.33, -6.25) * mm, "end": v(-2.3, -6.22) * mm});
            skLineSegment(sketch, "E346", {"start": v(-2.3, -6.22) * mm, "end": v(-2.28, -6.2) * mm});
            skLineSegment(sketch, "E347", {"start": v(-2.28, -6.2) * mm, "end": v(-2.27, -6.19) * mm});
            skLineSegment(sketch, "E348", {"start": v(-2.27, -6.19) * mm, "end": v(-1.07, -4.44) * mm});
            skLineSegment(sketch, "E349", {"start": v(-1.07, -4.44) * mm, "end": v(1.44, -5.68) * mm});
            skLineSegment(sketch, "E350", {"start": v(1.44, -5.68) * mm, "end": v(0.78, -7.7) * mm});
            skLineSegment(sketch, "E351", {"start": v(0.78, -7.7) * mm, "end": v(0.78, -7.72) * mm});
            skLineSegment(sketch, "E352", {"start": v(0.78, -7.72) * mm, "end": v(0.77, -7.74) * mm});
            skLineSegment(sketch, "E353", {"start": v(0.77, -7.74) * mm, "end": v(0.76, -7.79) * mm});
            skLineSegment(sketch, "E354", {"start": v(0.76, -7.79) * mm, "end": v(0.75, -7.84) * mm});
            skLineSegment(sketch, "E355", {"start": v(0.75, -7.84) * mm, "end": v(0.74, -7.91) * mm});
            skLineSegment(sketch, "E356", {"start": v(0.74, -7.91) * mm, "end": v(0.73, -8) * mm});
            skLineSegment(sketch, "E357", {"start": v(0.73, -8) * mm, "end": v(0.73, -8.1) * mm});
            skLineSegment(sketch, "E358", {"start": v(0.73, -8.1) * mm, "end": v(0.72, -8.21) * mm});
            skLineSegment(sketch, "E359", {"start": v(0.72, -8.21) * mm, "end": v(0.72, -8.34) * mm});
            skLineSegment(sketch, "E360", {"start": v(0.72, -8.34) * mm, "end": v(0.73, -8.48) * mm});
            skLineSegment(sketch, "E361", {"start": v(0.73, -8.48) * mm, "end": v(0.74, -8.64) * mm});
            skLineSegment(sketch, "E362", {"start": v(0.74, -8.64) * mm, "end": v(0.76, -8.81) * mm});
            skLineSegment(sketch, "E363", {"start": v(0.76, -8.81) * mm, "end": v(0.78, -9) * mm});
            skLineSegment(sketch, "E364", {"start": v(0.78, -9) * mm, "end": v(0.82, -9.2) * mm});
            skLineSegment(sketch, "E365", {"start": v(0.82, -9.2) * mm, "end": v(0.86, -9.4) * mm});
            skLineSegment(sketch, "E366", {"start": v(0.86, -9.4) * mm, "end": v(0.92, -9.63) * mm});
            skLineSegment(sketch, "E367", {"start": v(0.92, -9.63) * mm, "end": v(0.98, -9.86) * mm});
            skLineSegment(sketch, "E368", {"start": v(0.98, -9.86) * mm, "end": v(1.06, -10.1) * mm});
            skLineSegment(sketch, "E369", {"start": v(1.06, -10.1) * mm, "end": v(1.16, -10.36) * mm});
            skLineSegment(sketch, "E370", {"start": v(1.16, -10.36) * mm, "end": v(1.26, -10.63) * mm});
            skLineSegment(sketch, "E371", {"start": v(1.26, -10.63) * mm, "end": v(1.39, -10.9) * mm});
            skLineSegment(sketch, "E372", {"start": v(1.39, -10.9) * mm, "end": v(1.52, -11.18) * mm});
            skLineSegment(sketch, "E373", {"start": v(1.52, -11.18) * mm, "end": v(1.71, -11.28) * mm});
            skLineSegment(sketch, "E374", {"start": v(1.71, -11.28) * mm, "end": v(2.76, -11.44) * mm});
            skLineSegment(sketch, "E375", {"start": v(2.76, -11.44) * mm, "end": v(2.97, -11.4) * mm});
            skLineSegment(sketch, "E376", {"start": v(2.97, -11.4) * mm, "end": v(3.18, -11.16) * mm});
            skLineSegment(sketch, "E377", {"start": v(3.18, -11.16) * mm, "end": v(3.38, -10.94) * mm});
            skLineSegment(sketch, "E378", {"start": v(3.38, -10.94) * mm, "end": v(3.56, -10.71) * mm});
            skLineSegment(sketch, "E379", {"start": v(3.56, -10.71) * mm, "end": v(3.72, -10.5) * mm});
            skLineSegment(sketch, "E380", {"start": v(3.72, -10.5) * mm, "end": v(3.87, -10.28) * mm});
            skLineSegment(sketch, "E381", {"start": v(3.87, -10.28) * mm, "end": v(4, -10.08) * mm});
            skLineSegment(sketch, "E382", {"start": v(4, -10.08) * mm, "end": v(4.11, -9.88) * mm});
            skLineSegment(sketch, "E383", {"start": v(4.11, -9.88) * mm, "end": v(4.22, -9.7) * mm});
            skLineSegment(sketch, "E384", {"start": v(4.22, -9.7) * mm, "end": v(4.3, -9.51) * mm});
            skLineSegment(sketch, "E385", {"start": v(4.3, -9.51) * mm, "end": v(4.39, -9.34) * mm});
            skLineSegment(sketch, "E386", {"start": v(4.39, -9.34) * mm, "end": v(4.45, -9.19) * mm});
            skLineSegment(sketch, "E387", {"start": v(4.45, -9.19) * mm, "end": v(4.5, -9.04) * mm});
            skLineSegment(sketch, "E388", {"start": v(4.5, -9.04) * mm, "end": v(4.55, -8.9) * mm});
            skLineSegment(sketch, "E389", {"start": v(4.55, -8.9) * mm, "end": v(4.59, -8.78) * mm});
            skLineSegment(sketch, "E390", {"start": v(4.59, -8.78) * mm, "end": v(4.62, -8.67) * mm});
            skLineSegment(sketch, "E391", {"start": v(4.62, -8.67) * mm, "end": v(4.64, -8.57) * mm});
            skLineSegment(sketch, "E392", {"start": v(4.64, -8.57) * mm, "end": v(4.66, -8.49) * mm});
            skLineSegment(sketch, "E393", {"start": v(4.66, -8.49) * mm, "end": v(4.67, -8.42) * mm});
            skLineSegment(sketch, "E394", {"start": v(4.67, -8.42) * mm, "end": v(4.67, -8.36) * mm});
            skLineSegment(sketch, "E395", {"start": v(4.67, -8.36) * mm, "end": v(4.68, -8.32) * mm});
            skLineSegment(sketch, "E396", {"start": v(4.68, -8.32) * mm, "end": v(4.68, -8.29) * mm});
            skLineSegment(sketch, "E397", {"start": v(4.68, -8.29) * mm, "end": v(4.68, -8.27) * mm});
            skLineSegment(sketch, "E398", {"start": v(4.68, -8.27) * mm, "end": v(4.63, -6.15) * mm});
            skLineSegment(sketch, "E399", {"start": v(4.63, -6.15) * mm, "end": v(7.39, -5.68) * mm});
            skLineSegment(sketch, "E400", {"start": v(7.39, -5.68) * mm, "end": v(8.04, -7.7) * mm});
            skLineSegment(sketch, "E401", {"start": v(8.04, -7.7) * mm, "end": v(8.05, -7.72) * mm});
            skLineSegment(sketch, "E402", {"start": v(8.05, -7.72) * mm, "end": v(8.06, -7.74) * mm});
            skLineSegment(sketch, "E403", {"start": v(8.06, -7.74) * mm, "end": v(8.08, -7.78) * mm});
            skLineSegment(sketch, "E404", {"start": v(8.08, -7.78) * mm, "end": v(8.1, -7.83) * mm});
            skLineSegment(sketch, "E405", {"start": v(8.1, -7.83) * mm, "end": v(8.13, -7.9) * mm});
            skLineSegment(sketch, "E406", {"start": v(8.13, -7.9) * mm, "end": v(8.18, -7.97) * mm});
            skLineSegment(sketch, "E407", {"start": v(8.18, -7.97) * mm, "end": v(8.23, -8.05) * mm});
            skLineSegment(sketch, "E408", {"start": v(8.23, -8.05) * mm, "end": v(8.3, -8.15) * mm});
            skLineSegment(sketch, "E409", {"start": v(8.3, -8.15) * mm, "end": v(8.37, -8.25) * mm});
            skLineSegment(sketch, "E410", {"start": v(8.37, -8.25) * mm, "end": v(8.46, -8.37) * mm});
            skLineSegment(sketch, "E411", {"start": v(8.46, -8.37) * mm, "end": v(8.56, -8.49) * mm});
            skLineSegment(sketch, "E412", {"start": v(8.56, -8.49) * mm, "end": v(8.67, -8.61) * mm});
            skLineSegment(sketch, "E413", {"start": v(8.67, -8.61) * mm, "end": v(8.8, -8.75) * mm});
            skLineSegment(sketch, "E414", {"start": v(8.8, -8.75) * mm, "end": v(8.95, -8.89) * mm});
            skLineSegment(sketch, "E415", {"start": v(8.95, -8.89) * mm, "end": v(9.1, -9.03) * mm});
            skLineSegment(sketch, "E416", {"start": v(9.1, -9.03) * mm, "end": v(9.28, -9.18) * mm});
            skLineSegment(sketch, "E417", {"start": v(9.28, -9.18) * mm, "end": v(9.47, -9.33) * mm});
            skLineSegment(sketch, "E418", {"start": v(9.47, -9.33) * mm, "end": v(9.68, -9.48) * mm});
            skLineSegment(sketch, "E419", {"start": v(9.68, -9.48) * mm, "end": v(9.9, -9.63) * mm});
            skLineSegment(sketch, "E420", {"start": v(9.9, -9.63) * mm, "end": v(10.15, -9.78) * mm});
            skLineSegment(sketch, "E421", {"start": v(10.15, -9.78) * mm, "end": v(10.41, -9.93) * mm});
            skLineSegment(sketch, "E422", {"start": v(10.41, -9.93) * mm, "end": v(10.69, -10.08) * mm});
            skLineSegment(sketch, "E423", {"start": v(10.69, -10.08) * mm, "end": v(10.9, -10.05) * mm});
            skLineSegment(sketch, "E424", {"start": v(10.9, -10.05) * mm, "end": v(11.84, -9.56) * mm});
            skLineSegment(sketch, "E425", {"start": v(11.84, -9.56) * mm, "end": v(11.98, -9.4) * mm});
            skLineSegment(sketch, "E426", {"start": v(11.98, -9.4) * mm, "end": v(12.02, -9.1) * mm});
            skLineSegment(sketch, "E427", {"start": v(12.02, -9.1) * mm, "end": v(12.04, -8.8) * mm});
            skLineSegment(sketch, "E428", {"start": v(12.04, -8.8) * mm, "end": v(12.06, -8.5) * mm});
            skLineSegment(sketch, "E429", {"start": v(12.06, -8.5) * mm, "end": v(12.06, -8.23) * mm});
            skLineSegment(sketch, "E430", {"start": v(12.06, -8.23) * mm, "end": v(12.05, -7.98) * mm});
            skLineSegment(sketch, "E431", {"start": v(12.05, -7.98) * mm, "end": v(12.04, -7.73) * mm});
            skLineSegment(sketch, "E432", {"start": v(12.04, -7.73) * mm, "end": v(12.02, -7.5) * mm});
            skLineSegment(sketch, "E433", {"start": v(12.02, -7.5) * mm, "end": v(12, -7.3) * mm});
            skLineSegment(sketch, "E434", {"start": v(12, -7.3) * mm, "end": v(11.96, -7.1) * mm});
            skLineSegment(sketch, "E435", {"start": v(11.96, -7.1) * mm, "end": v(11.92, -6.91) * mm});
            skLineSegment(sketch, "E436", {"start": v(11.92, -6.91) * mm, "end": v(11.88, -6.74) * mm});
            skLineSegment(sketch, "E437", {"start": v(11.88, -6.74) * mm, "end": v(11.84, -6.6) * mm});
            skLineSegment(sketch, "E438", {"start": v(11.84, -6.6) * mm, "end": v(11.8, -6.46) * mm});
            skLineSegment(sketch, "E439", {"start": v(11.8, -6.46) * mm, "end": v(11.76, -6.34) * mm});
            skLineSegment(sketch, "E440", {"start": v(11.76, -6.34) * mm, "end": v(11.72, -6.23) * mm});
            skLineSegment(sketch, "E441", {"start": v(11.72, -6.23) * mm, "end": v(11.68, -6.14) * mm});
            skLineSegment(sketch, "E442", {"start": v(11.68, -6.14) * mm, "end": v(11.64, -6.06) * mm});
            skLineSegment(sketch, "E443", {"start": v(11.64, -6.06) * mm, "end": v(11.6, -6) * mm});
            skLineSegment(sketch, "E444", {"start": v(11.6, -6) * mm, "end": v(11.58, -5.95) * mm});
            skLineSegment(sketch, "E445", {"start": v(11.58, -5.95) * mm, "end": v(11.56, -5.9) * mm});
            skLineSegment(sketch, "E446", {"start": v(11.56, -5.9) * mm, "end": v(11.54, -5.88) * mm});
            skLineSegment(sketch, "E447", {"start": v(11.54, -5.88) * mm, "end": v(11.53, -5.87) * mm});
            skLineSegment(sketch, "E448", {"start": v(11.53, -5.87) * mm, "end": v(10.25, -4.18) * mm});
            skLineSegment(sketch, "E449", {"start": v(10.25, -4.18) * mm, "end": v(12.2, -2.19) * mm});
            skLineSegment(sketch, "E450", {"start": v(12.2, -2.19) * mm, "end": v(13.92, -3.43) * mm});
            skLineSegment(sketch, "E451", {"start": v(13.92, -3.43) * mm, "end": v(13.93, -3.44) * mm});
            skLineSegment(sketch, "E452", {"start": v(13.93, -3.44) * mm, "end": v(13.95, -3.46) * mm});
            skLineSegment(sketch, "E453", {"start": v(13.95, -3.46) * mm, "end": v(13.99, -3.48) * mm});
            skLineSegment(sketch, "E454", {"start": v(13.99, -3.48) * mm, "end": v(14.04, -3.5) * mm});
            skLineSegment(sketch, "E455", {"start": v(14.04, -3.5) * mm, "end": v(14.1, -3.54) * mm});
            skLineSegment(sketch, "E456", {"start": v(14.1, -3.54) * mm, "end": v(14.18, -3.57) * mm});
            skLineSegment(sketch, "E457", {"start": v(14.18, -3.57) * mm, "end": v(14.28, -3.6) * mm});
            skLineSegment(sketch, "E458", {"start": v(14.28, -3.6) * mm, "end": v(14.38, -3.65) * mm});
            skLineSegment(sketch, "E459", {"start": v(14.38, -3.65) * mm, "end": v(14.5, -3.69) * mm});
            skLineSegment(sketch, "E460", {"start": v(14.5, -3.69) * mm, "end": v(14.64, -3.73) * mm});
            skLineSegment(sketch, "E461", {"start": v(14.64, -3.73) * mm, "end": v(14.8, -3.77) * mm});
            skLineSegment(sketch, "E462", {"start": v(14.8, -3.77) * mm, "end": v(14.96, -3.8) * mm});
            skLineSegment(sketch, "E463", {"start": v(14.96, -3.8) * mm, "end": v(15.15, -3.83) * mm});
            skLineSegment(sketch, "E464", {"start": v(15.15, -3.83) * mm, "end": v(15.35, -3.86) * mm});
            skLineSegment(sketch, "E465", {"start": v(15.35, -3.86) * mm, "end": v(15.56, -3.88) * mm});
            skLineSegment(sketch, "E466", {"start": v(15.56, -3.88) * mm, "end": v(15.79, -3.9) * mm});
            skLineSegment(sketch, "E467", {"start": v(15.79, -3.9) * mm, "end": v(16.03, -3.9) * mm});
            skLineSegment(sketch, "E468", {"start": v(16.03, -3.9) * mm, "end": v(16.29, -3.9) * mm});
            skLineSegment(sketch, "E469", {"start": v(16.29, -3.9) * mm, "end": v(16.56, -3.9) * mm});
            skLineSegment(sketch, "E470", {"start": v(16.56, -3.9) * mm, "end": v(16.85, -3.88) * mm});
            skLineSegment(sketch, "E471", {"start": v(16.85, -3.88) * mm, "end": v(17.14, -3.85) * mm});
            skLineSegment(sketch, "E472", {"start": v(17.14, -3.85) * mm, "end": v(17.46, -3.8) * mm});
            skLineSegment(sketch, "E473", {"start": v(17.46, -3.8) * mm, "end": v(17.61, -3.65) * mm});
            skLineSegment(sketch, "E474", {"start": v(17.61, -3.65) * mm, "end": v(18.08, -2.7) * mm});
            skLineSegment(sketch, "E475", {"start": v(18.08, -2.7) * mm, "end": v(18.1, -2.5) * mm});
            skLineSegment(sketch, "E476", {"start": v(18.1, -2.5) * mm, "end": v(17.95, -2.22) * mm});
            skLineSegment(sketch, "E477", {"start": v(17.95, -2.22) * mm, "end": v(17.8, -1.96) * mm});
            skLineSegment(sketch, "E478", {"start": v(17.8, -1.96) * mm, "end": v(17.64, -1.72) * mm});
            skLineSegment(sketch, "E479", {"start": v(17.64, -1.72) * mm, "end": v(17.48, -1.5) * mm});
            skLineSegment(sketch, "E480", {"start": v(17.48, -1.5) * mm, "end": v(17.32, -1.3) * mm});
            skLineSegment(sketch, "E481", {"start": v(17.32, -1.3) * mm, "end": v(17.17, -1.1) * mm});
            skLineSegment(sketch, "E482", {"start": v(17.17, -1.1) * mm, "end": v(17.02, -0.94) * mm});
            skLineSegment(sketch, "E483", {"start": v(17.02, -0.94) * mm, "end": v(16.87, -0.78) * mm});
            skLineSegment(sketch, "E484", {"start": v(16.87, -0.78) * mm, "end": v(16.73, -0.64) * mm});
            skLineSegment(sketch, "E485", {"start": v(16.73, -0.64) * mm, "end": v(16.6, -0.51) * mm});
            skLineSegment(sketch, "E486", {"start": v(16.6, -0.51) * mm, "end": v(16.46, -0.4) * mm});
            skLineSegment(sketch, "E487", {"start": v(16.46, -0.4) * mm, "end": v(16.34, -0.3) * mm});
            skLineSegment(sketch, "E488", {"start": v(16.34, -0.3) * mm, "end": v(16.22, -0.22) * mm});
            skLineSegment(sketch, "E489", {"start": v(16.22, -0.22) * mm, "end": v(16.12, -0.14) * mm});
            skLineSegment(sketch, "E490", {"start": v(16.12, -0.14) * mm, "end": v(16.02, -0.08) * mm});
            skLineSegment(sketch, "E491", {"start": v(16.02, -0.08) * mm, "end": v(15.94, -0.03) * mm});
            skLineSegment(sketch, "E492", {"start": v(15.94, -0.03) * mm, "end": v(15.86, 0) * mm});
            skLineSegment(sketch, "E493", {"start": v(15.86, 0) * mm, "end": v(15.8, 0.04) * mm});
            skLineSegment(sketch, "E494", {"start": v(15.8, 0.04) * mm, "end": v(15.74, 0.07) * mm});
            skLineSegment(sketch, "E495", {"start": v(15.74, 0.07) * mm, "end": v(15.7, 0.08) * mm});
            skLineSegment(sketch, "E496", {"start": v(15.7, 0.08) * mm, "end": v(15.68, 0.1) * mm});
            skLineSegment(sketch, "E497", {"start": v(15.68, 0.1) * mm, "end": v(15.66, 0.1) * mm});
            skLineSegment(sketch, "E498", {"start": v(15.66, 0.1) * mm, "end": v(13.63, 0.7) * mm});
            skLineSegment(sketch, "E499", {"start": v(13.63, 0.7) * mm, "end": v(14.04, 3.47) * mm});
            skLineSegment(sketch, "E500", {"start": v(5.54, 3.47) * mm, "end": v(3.29, 3.47) * mm});
            skLineSegment(sketch, "E501", {"start": v(4.41, 4.6) * mm, "end": v(4.41, 2.35) * mm});
            skFitSpline(sketch, "E502", {"points": [v(17.72, 5.57) * mm, v(17.72, 6.1) * mm, v(17.28, 6.55) * mm, v(16.73, 6.55) * mm, v(16.2, 6.55) * mm, v(15.75, 6.1) * mm, v(15.75, 5.57) * mm, v(15.75, 5.03) * mm, v(16.2, 4.59) * mm, v(16.73, 4.59) * mm, v(17.28, 4.59) * mm, v(17.72, 5.03) * mm, v(17.72, 5.57) * mm]});
            skCircle(sketch, "E503", {"center": v(4.41, 3.47) * mm, "radius": 2.5 * mm});
            skSolve(sketch);
        }
        {
            var Q0;
            Q0=makeQuery(id+"F0.imprint","IMPRINT",FACE,{"disambiguationData":[TD([[makeQuery(id+"F0.imprint","IMPRINT",EDGE,{"derivedFrom":sQuery(id+"F0.wireOp",EDGE,"E0")}),1.0]])]});
            extrude(context, id + "F1", {"entities" : qUnion([Q0]), "depth" : 5 * mm, "offsetDistance" : 25 * mm});
        }
    });
